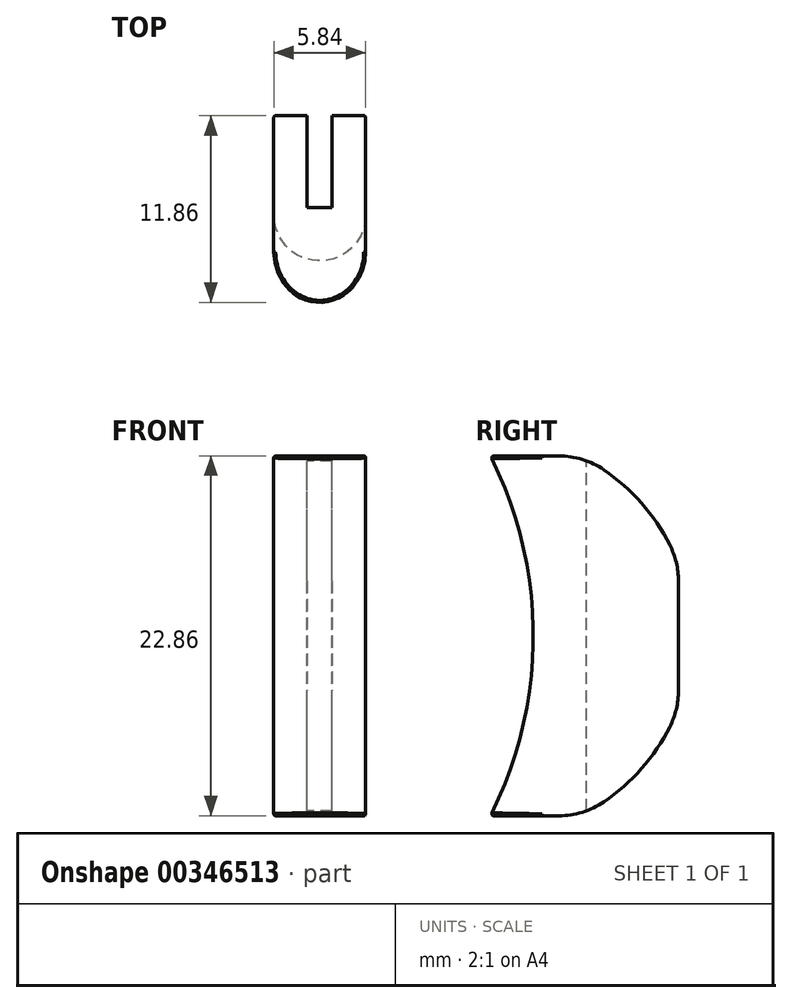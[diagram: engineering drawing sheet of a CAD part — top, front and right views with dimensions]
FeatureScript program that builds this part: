
annotation { "Feature Type Name" : "Feature", "Feature Type Description" : "" }
export const myFeature = defineFeature(function(context is Context, id is Id, definition is map)
    precondition{}
    {
        {
            var Q0;
            Q0=qCreatedBy(makeId("Right.planeOp"),FACE);
            var sketch = newSketch(context, id + "F0", { "sketchPlane" : qUnion([Q0])});
            skArc(sketch, "E0", {"start": v(22.68, 11.43) * mm, "mid": v(25.4, 0) * mm, "end": v(22.68, -11.43) * mm});
            skLineSegment(sketch, "E1", {"start": v(0, 0) * mm, "end": v(22.68, 0) * mm, "construction": true});
            skLineSegment(sketch, "E2", {"start": v(22.68, 11.43) * mm, "end": v(28.38, 11.43) * mm});
            skLineSegment(sketch, "E3.MirrorCS", {"start": v(22.68, -11.43) * mm, "end": v(28.38, -11.43) * mm});
            skLineSegment(sketch, "E4", {"start": v(22.68, 11.43) * mm, "end": v(22.68, -11.43) * mm, "construction": true});
            skLineSegment(sketch, "E5", {"start": v(34.62, 4.53) * mm, "end": v(34.62, -4.53) * mm});
            skLineSegment(sketch, "E6", {"start": v(22.68, 0) * mm, "end": v(34.62, 0) * mm, "construction": true});
            skArc(sketch, "E7", {"start": v(34.62, 4.53) * mm, "mid": v(32.15, 8.57) * mm, "end": v(28.38, 11.43) * mm});
            skArc(sketch, "E8.MirrorCS", {"start": v(34.62, -4.53) * mm, "mid": v(32.15, -8.57) * mm, "end": v(28.38, -11.43) * mm});
            skSolve(sketch);
        }
        {
            var Q0;
            Q0=qSketchRegion(id+"F0",true);
            extrude(context, id + "F1", {"entities" : qUnion([Q0]), "depth" : 5.84 * mm, "symmetric" : true});
        }
        {
            var Q0;
            Q0=qCreatedBy(makeId("Top.planeOp"),FACE);
            var sketch = newSketch(context, id + "F2", { "sketchPlane" : qUnion([Q0])});
            skLineSegment(sketch, "E9.0", {"start": v(2.92, 22.68) * mm, "end": v(-2.92, 22.68) * mm, "construction": true});
            skLineSegment(sketch, "E10", {"start": v(0, 22.68) * mm, "end": v(0, 36.06) * mm, "construction": true});
            skPoint(sketch, "E10.endSnap0", {"position": v(0, 22.68) * mm});
            skLineSegment(sketch, "E11.bottom", {"start": v(0.8, 28.78) * mm, "end": v(-0.8, 28.78) * mm});
            skLineSegment(sketch, "E11.top", {"start": v(0.8, 43.35) * mm, "end": v(-0.8, 43.35) * mm});
            skLineSegment(sketch, "E11.left", {"start": v(0.8, 28.78) * mm, "end": v(0.8, 43.35) * mm});
            skLineSegment(sketch, "E11.right", {"start": v(-0.8, 28.78) * mm, "end": v(-0.8, 43.35) * mm});
            skPoint(sketch, "E11.middle", {"position": v(0, 36.06) * mm});
            skSolve(sketch);
        }
        {
            var Q0;
            Q0=qSketchRegion(id+"F2",true);
            extrude(context, id + "F3", {"entities" : qUnion([Q0]), "operationType" : NewBodyOperationType.REMOVE, "oppositeDirection" : true, "depth" : 25.4 * mm, "symmetric" : true});
        }
        {
            var Q0;
            Q0=makeQuery(id+"F1.opExtrude","CAP_EDGE",EDGE,{"disambiguationData":[OSD([sQuery(id+"F0.wireOp",EDGE,"E0")])],"isStart":true});
            var Q1;
            Q1=makeQuery(id+"F1.opExtrude","CAP_EDGE",EDGE,{"disambiguationData":[OSD([sQuery(id+"F0.wireOp",EDGE,"E0")])],"isStart":false});
            fillet(context, id + "F4", {"entities" : qUnion([Q0, Q1]), "radius" : 2.92 * mm, "tangentPropagation" : true, "allowEdgeOverflow" : false});
        }
        {
            var Q0;
            Q0=makeQuery(id+"F1.opExtrude","SWEPT_EDGE",EDGE,{"disambiguationData":[OSD([sQuery(id+"F0.wireOp",EDGE,"E3.MirrorCS"),sQuery(id+"F0.wireOp",EDGE,"E8.MirrorCS")])]});
            var Q1;
            Q1=makeQuery(id+"F1.opExtrude","SWEPT_EDGE",EDGE,{"disambiguationData":[OSD([sQuery(id+"F0.wireOp",EDGE,"E2"),sQuery(id+"F0.wireOp",EDGE,"E7")])]});
            var Q2;
            {var subQ0=sQuery(id+"F0.wireOp",EDGE,"E7");var subQ1=sQuery(id+"F0.wireOp",EDGE,"E5");Q2=makeQuery(id+"F3.boolean.opBoolean","SPLIT",EDGE,{"disambiguationData":[TD([makeQuery(id+"F3.opExtrude","SWEPT_FACE",FACE,{"disambiguationData":[OSD([sQuery(id+"F2.wireOp",EDGE,"E11.left")])]})])],"derivedFrom":makeQuery(id+"F1.opExtrude","SWEPT_EDGE",EDGE,{"disambiguationData":[OSD([subQ1,subQ0])]})});}
            var Q3;
            {var subQ0=sQuery(id+"F0.wireOp",EDGE,"E7");var subQ1=sQuery(id+"F0.wireOp",EDGE,"E5");Q3=makeQuery(id+"F3.boolean.opBoolean","SPLIT",EDGE,{"disambiguationData":[TD([makeQuery(id+"F3.opExtrude","SWEPT_FACE",FACE,{"disambiguationData":[OSD([sQuery(id+"F2.wireOp",EDGE,"E11.right")])]})])],"derivedFrom":makeQuery(id+"F1.opExtrude","SWEPT_EDGE",EDGE,{"disambiguationData":[OSD([subQ1,subQ0])]})});}
            var Q4;
            {var subQ0=sQuery(id+"F0.wireOp",EDGE,"E8.MirrorCS");var subQ1=sQuery(id+"F0.wireOp",EDGE,"E5");Q4=makeQuery(id+"F3.boolean.opBoolean","SPLIT",EDGE,{"disambiguationData":[TD([makeQuery(id+"F3.opExtrude","SWEPT_FACE",FACE,{"disambiguationData":[OSD([sQuery(id+"F2.wireOp",EDGE,"E11.left")])]})])],"derivedFrom":makeQuery(id+"F1.opExtrude","SWEPT_EDGE",EDGE,{"disambiguationData":[OSD([subQ1,subQ0])]})});}
            var Q5;
            {var subQ0=sQuery(id+"F0.wireOp",EDGE,"E8.MirrorCS");var subQ1=sQuery(id+"F0.wireOp",EDGE,"E5");Q5=makeQuery(id+"F3.boolean.opBoolean","SPLIT",EDGE,{"disambiguationData":[TD([makeQuery(id+"F3.opExtrude","SWEPT_FACE",FACE,{"disambiguationData":[OSD([sQuery(id+"F2.wireOp",EDGE,"E11.right")])]})])],"derivedFrom":makeQuery(id+"F1.opExtrude","SWEPT_EDGE",EDGE,{"disambiguationData":[OSD([subQ1,subQ0])]})});}
            fillet(context, id + "F5", {"entities" : qUnion([Q0, Q1, Q2, Q3, Q4, Q5]), "radius" : 5.08 * mm, "tangentPropagation" : true, "allowEdgeOverflow" : false});
        }
        {
            var Q0;
            Q0=makeQuery(id+"F1.opExtrude","CAP_EDGE",EDGE,{"disambiguationData":[OSD([sQuery(id+"F0.wireOp",EDGE,"E7")])],"isStart":true});
            fillet(context, id + "F6", {"entities" : qUnion([Q0]), "radius" : 0.13 * mm, "tangentPropagation" : true, "allowEdgeOverflow" : false});
        }
    });
